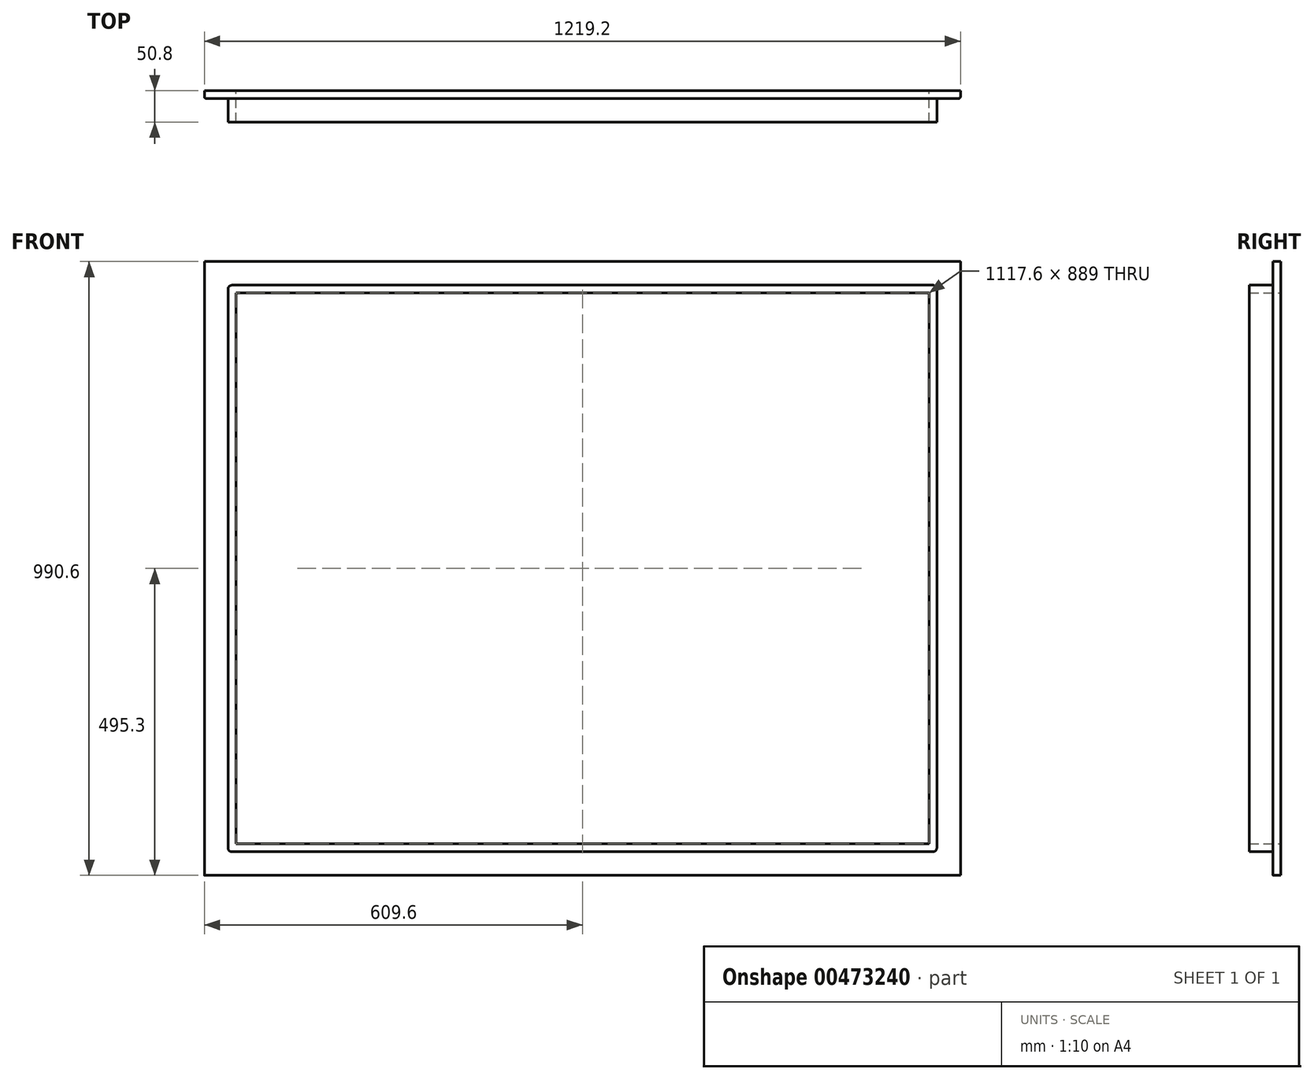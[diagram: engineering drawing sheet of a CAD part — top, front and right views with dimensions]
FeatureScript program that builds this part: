
annotation { "Feature Type Name" : "Feature", "Feature Type Description" : "" }
export const myFeature = defineFeature(function(context is Context, id is Id, definition is map)
    precondition{}
    {
        {
            var Q0;
            Q0=qCreatedBy(makeId("Front.planeOp"),FACE);
            var sketch = newSketch(context, id + "F0", { "sketchPlane" : qUnion([Q0])});
            skLineSegment(sketch, "E0.bottom", {"start": v(609.6, 495.3) * mm, "end": v(-609.6, 495.3) * mm});
            skLineSegment(sketch, "E0.top", {"start": v(609.6, -495.3) * mm, "end": v(-609.6, -495.3) * mm});
            skLineSegment(sketch, "E0.left", {"start": v(609.6, 495.3) * mm, "end": v(609.6, -495.3) * mm});
            skLineSegment(sketch, "E0.right", {"start": v(-609.6, 495.3) * mm, "end": v(-609.6, -495.3) * mm});
            skPoint(sketch, "E0.middle", {"position": v(0, 0) * mm});
            skLineSegment(sketch, "E1.bottom", {"start": v(558.8, 444.5) * mm, "end": v(-558.8, 444.5) * mm});
            skLineSegment(sketch, "E1.top", {"start": v(558.8, -444.5) * mm, "end": v(-558.8, -444.5) * mm});
            skLineSegment(sketch, "E1.left", {"start": v(558.8, 444.5) * mm, "end": v(558.8, -444.5) * mm});
            skLineSegment(sketch, "E1.right", {"start": v(-558.8, 444.5) * mm, "end": v(-558.8, -444.5) * mm});
            skLineSegment(sketch, "E2.bottom", {"start": v(565.15, -457.2) * mm, "end": v(-565.15, -457.2) * mm});
            skLineSegment(sketch, "E2.top", {"start": v(565.15, 457.2) * mm, "end": v(-565.15, 457.2) * mm});
            skLineSegment(sketch, "E2.left", {"start": v(571.5, -450.85) * mm, "end": v(571.5, 450.85) * mm});
            skLineSegment(sketch, "E2.right", {"start": v(-571.5, -450.85) * mm, "end": v(-571.5, 450.85) * mm});
            skPoint(sketch, "E3.visualSharp", {"position": v(571.5, 457.2) * mm});
            skArc(sketch, "E3.filletArc", {"start": v(571.5, 450.85) * mm, "mid": v(569.64, 455.34) * mm, "end": v(565.15, 457.2) * mm});
            skPoint(sketch, "E4.visualSharp", {"position": v(571.5, -457.2) * mm});
            skArc(sketch, "E4.filletArc", {"start": v(565.15, -457.2) * mm, "mid": v(569.64, -455.34) * mm, "end": v(571.5, -450.85) * mm});
            skPoint(sketch, "E5.visualSharp", {"position": v(-571.5, -457.2) * mm});
            skArc(sketch, "E5.filletArc", {"start": v(-571.5, -450.85) * mm, "mid": v(-569.64, -455.34) * mm, "end": v(-565.15, -457.2) * mm});
            skPoint(sketch, "E6.visualSharp", {"position": v(-571.5, 457.2) * mm});
            skArc(sketch, "E6.filletArc", {"start": v(-565.15, 457.2) * mm, "mid": v(-569.64, 455.34) * mm, "end": v(-571.5, 450.85) * mm});
            skSolve(sketch);
        }
        {
            var Q0;
            Q0=makeQuery(id+"F0.imprint","IMPRINT",FACE,{"disambiguationData":[TD([[makeQuery(id+"F0.imprint","IMPRINT",EDGE,{"derivedFrom":sQuery(id+"F0.wireOp",EDGE,"E1.bottom")}),-1.0]])]});
            extrude(context, id + "F1", {"entities" : qUnion([Q0]), "depth" : 50.8 * mm});
        }
        {
            var Q0;
            Q0=makeQuery(id+"F0.imprint","IMPRINT",FACE,{"disambiguationData":[TD([[makeQuery(id+"F0.imprint","IMPRINT",EDGE,{"derivedFrom":sQuery(id+"F0.wireOp",EDGE,"E0.bottom")}),1.0]])]});
            extrude(context, id + "F2", {"entities" : qUnion([Q0]), "operationType" : NewBodyOperationType.ADD, "depth" : 12.7 * mm});
        }
        {
            var Q0;
            Q0=makeQuery(id+"F2.opExtrude","CAP_EDGE",EDGE,{"disambiguationData":[OSD([sQuery(id+"F0.wireOp",EDGE,"E0.right")])],"isStart":false});
            var Q1;
            Q1=makeQuery(id+"F2.opExtrude","CAP_EDGE",EDGE,{"disambiguationData":[OSD([sQuery(id+"F0.wireOp",EDGE,"E0.left")])],"isStart":false});
            fillet(context, id + "F3", {"entities" : qUnion([Q0, Q1]), "radius" : 3.17 * mm, "tangentPropagation" : true, "allowEdgeOverflow" : false});
        }
    });
